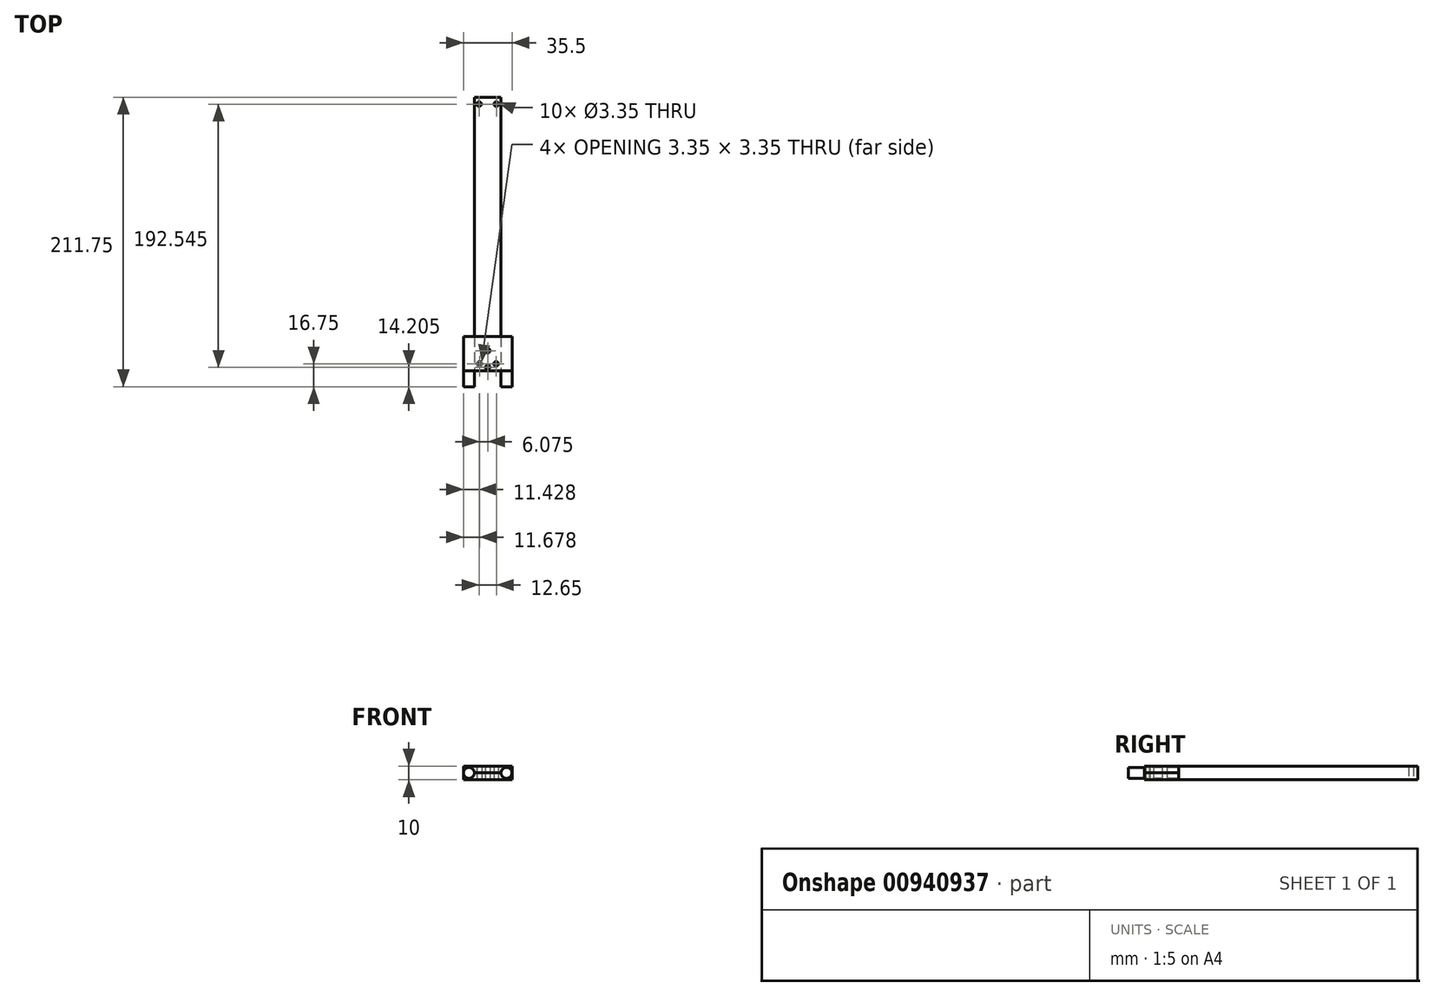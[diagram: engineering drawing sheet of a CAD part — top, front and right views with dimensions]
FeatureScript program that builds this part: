
annotation { "Feature Type Name" : "Feature", "Feature Type Description" : "" }
export const myFeature = defineFeature(function(context is Context, id is Id, definition is map)
    precondition{}
    {
        {
            var Q0;
            Q0=qCreatedBy(makeId("Front.planeOp"),FACE);
            var sketch = newSketch(context, id + "F0", { "sketchPlane" : qUnion([Q0])});
            skLineSegment(sketch, "E0.bottom", {"start": v(-75.87, 17.55) * mm, "end": v(-111.37, 17.55) * mm});
            skLineSegment(sketch, "E0.top", {"start": v(-75.87, 7.55) * mm, "end": v(-111.37, 7.55) * mm});
            skLineSegment(sketch, "E0.left", {"start": v(-75.87, 17.55) * mm, "end": v(-75.87, 7.55) * mm});
            skLineSegment(sketch, "E0.right", {"start": v(-111.37, 17.55) * mm, "end": v(-111.37, 7.55) * mm});
            skLineSegment(sketch, "E1", {"start": v(-75.87, 12.55) * mm, "end": v(-111.37, 12.55) * mm});
            skLineSegment(sketch, "E2", {"start": v(-111.37, 12.55) * mm, "end": v(-107.37, 12.55) * mm});
            skLineSegment(sketch, "E3", {"start": v(-107.37, 12.55) * mm, "end": v(-75.87, 12.55) * mm});
            skLineSegment(sketch, "E4", {"start": v(-75.87, 12.55) * mm, "end": v(-79.87, 12.55) * mm});
            skCircle(sketch, "E5", {"center": v(-107.37, 12.55) * mm, "radius": 4 * mm});
            skCircle(sketch, "E6", {"center": v(-79.87, 12.55) * mm, "radius": 4 * mm});
            skSolve(sketch);
        }
        {
            var Q0;
            {var subQ1=sQuery(id+"F0.wireOp",EDGE,"E1");var subQ3=makeQuery(id+"F0.imprint","IMPRINT",VERTEX,{"disambiguationData":[OD(1.0)],"derivedFrom":subQ1});Q0=makeQuery(id+"F0.imprint","IMPRINT",FACE,{"disambiguationData":[TD([[makeQuery(id+"F0.imprint","IMPRINT",EDGE,{"disambiguationData":[TD([[subQ3,1.0]])],"derivedFrom":subQ1}),-1.0]])]});}
            var Q1;
            {var subQ1=sQuery(id+"F0.wireOp",EDGE,"E1");var subQ3=makeQuery(id+"F0.imprint","IMPRINT",VERTEX,{"disambiguationData":[OD(1.0)],"derivedFrom":subQ1});Q1=makeQuery(id+"F0.imprint","IMPRINT",FACE,{"disambiguationData":[TD([[makeQuery(id+"F0.imprint","IMPRINT",EDGE,{"disambiguationData":[TD([[subQ3,1.0]])],"derivedFrom":subQ1}),1.0]])]});}
            var Q2;
            {var subQ1=sQuery(id+"F0.wireOp",EDGE,"E1");var subQ3=makeQuery(id+"F0.imprint","IMPRINT",VERTEX,{"disambiguationData":[OD(0.0)],"derivedFrom":subQ1});Q2=makeQuery(id+"F0.imprint","IMPRINT",FACE,{"disambiguationData":[TD([[makeQuery(id+"F0.imprint","IMPRINT",EDGE,{"disambiguationData":[TD([[subQ3,-1.0]])],"derivedFrom":subQ1}),-1.0]])]});}
            var Q3;
            {var subQ1=sQuery(id+"F0.wireOp",EDGE,"E1");var subQ3=makeQuery(id+"F0.imprint","IMPRINT",VERTEX,{"disambiguationData":[OD(0.0)],"derivedFrom":subQ1});Q3=makeQuery(id+"F0.imprint","IMPRINT",FACE,{"disambiguationData":[TD([[makeQuery(id+"F0.imprint","IMPRINT",EDGE,{"disambiguationData":[TD([[subQ3,-1.0]])],"derivedFrom":subQ1}),1.0]])]});}
            extrude(context, id + "F1", {"entities" : qUnion([Q0, Q1, Q2, Q3]), "depth" : 11.75 * mm, "offsetDistance" : 25 * mm});
        }
        {
            var Q0;
            {var subQ1=sQuery(id+"F0.wireOp",EDGE,"E0.top");Q0=makeQuery(id+"F0.imprint","IMPRINT",FACE,{"disambiguationData":[TD([[makeQuery(id+"F0.imprint","IMPRINT",EDGE,{"derivedFrom":subQ1}),-1.0]])]});}
            extrude(context, id + "F2", {"entities" : qUnion([Q0]), "oppositeDirection" : true, "depth" : 25 * mm, "offsetDistance" : 25 * mm});
        }
        {
            var Q0;
            {var subQ6=sQuery(id+"F0.wireOp",EDGE,"E0.bottom");Q0=makeQuery(id+"F0.imprint","IMPRINT",FACE,{"disambiguationData":[TD([[makeQuery(id+"F0.imprint","IMPRINT",EDGE,{"derivedFrom":subQ6}),1.0]])]});}
            extrude(context, id + "F3", {"entities" : qUnion([Q0]), "oppositeDirection" : true, "depth" : 25 * mm, "offsetDistance" : 25 * mm});
        }
        {
            var Q0;
            {var subQ1=sQuery(id+"F0.wireOp",EDGE,"E1");var subQ3=makeQuery(id+"F0.imprint","IMPRINT",VERTEX,{"disambiguationData":[OD(1.0)],"derivedFrom":subQ1});Q0=makeQuery(id+"F0.imprint","IMPRINT",FACE,{"disambiguationData":[TD([[makeQuery(id+"F0.imprint","IMPRINT",EDGE,{"disambiguationData":[TD([[subQ3,1.0]])],"derivedFrom":subQ1}),-1.0]])]});}
            var Q1;
            {var subQ1=sQuery(id+"F0.wireOp",EDGE,"E1");var subQ3=makeQuery(id+"F0.imprint","IMPRINT",VERTEX,{"disambiguationData":[OD(1.0)],"derivedFrom":subQ1});Q1=makeQuery(id+"F0.imprint","IMPRINT",FACE,{"disambiguationData":[TD([[makeQuery(id+"F0.imprint","IMPRINT",EDGE,{"disambiguationData":[TD([[subQ3,1.0]])],"derivedFrom":subQ1}),1.0]])]});}
            var Q2;
            {var subQ1=sQuery(id+"F0.wireOp",EDGE,"E1");var subQ3=makeQuery(id+"F0.imprint","IMPRINT",VERTEX,{"disambiguationData":[OD(0.0)],"derivedFrom":subQ1});Q2=makeQuery(id+"F0.imprint","IMPRINT",FACE,{"disambiguationData":[TD([[makeQuery(id+"F0.imprint","IMPRINT",EDGE,{"disambiguationData":[TD([[subQ3,-1.0]])],"derivedFrom":subQ1}),-1.0]])]});}
            var Q3;
            {var subQ1=sQuery(id+"F0.wireOp",EDGE,"E1");var subQ3=makeQuery(id+"F0.imprint","IMPRINT",VERTEX,{"disambiguationData":[OD(0.0)],"derivedFrom":subQ1});Q3=makeQuery(id+"F0.imprint","IMPRINT",FACE,{"disambiguationData":[TD([[makeQuery(id+"F0.imprint","IMPRINT",EDGE,{"disambiguationData":[TD([[subQ3,-1.0]])],"derivedFrom":subQ1}),1.0]])]});}
            extrude(context, id + "F4", {"entities" : qUnion([Q0, Q1, Q2, Q3]), "oppositeDirection" : true, "depth" : 25 * mm, "offsetDistance" : 25 * mm});
        }
        {
            var Q0;
            Q0=makeQuery(id+"F3.opExtrude","CAP_FACE",FACE,{"disambiguationData":[OSD([sQuery(id+"F0.wireOp",EDGE,"E0.bottom"),sQuery(id+"F0.wireOp",EDGE,"E0.left"),sQuery(id+"F0.wireOp",EDGE,"E0.right"),sQuery(id+"F0.wireOp",EDGE,"E1"),sQuery(id+"F0.wireOp",EDGE,"E5"),sQuery(id+"F0.wireOp",EDGE,"E6")])],"isStart":false});
            var sketch = newSketch(context, id + "F5", { "sketchPlane" : qUnion([Q0])});
            skLineSegment(sketch, "E7.bottom", {"start": v(109.37, 7.55) * mm, "end": v(75.87, 7.55) * mm});
            skLineSegment(sketch, "E7.top", {"start": v(109.37, 17.55) * mm, "end": v(75.87, 17.55) * mm});
            skLineSegment(sketch, "E7.left", {"start": v(109.37, 7.55) * mm, "end": v(109.37, 17.55) * mm});
            skLineSegment(sketch, "E7.right", {"start": v(75.87, 7.55) * mm, "end": v(75.87, 17.55) * mm});
            skLineSegment(sketch, "E8", {"start": v(75.87, 12.55) * mm, "end": v(111.37, 12.55) * mm});
            skLineSegment(sketch, "E9", {"start": v(111.37, 12.55) * mm, "end": v(103.37, 12.55) * mm});
            skLineSegment(sketch, "E10", {"start": v(103.37, 12.55) * mm, "end": v(83.87, 12.55) * mm});
            skLineSegment(sketch, "E11", {"start": v(83.87, 12.55) * mm, "end": v(75.87, 12.55) * mm});
            skLineSegment(sketch, "E12", {"start": v(103.37, 12.55) * mm, "end": v(103.37, 7.55) * mm});
            skLineSegment(sketch, "E13", {"start": v(103.37, 7.55) * mm, "end": v(103.37, 17.55) * mm});
            skLineSegment(sketch, "E14", {"start": v(103.37, 17.55) * mm, "end": v(83.87, 17.55) * mm});
            skLineSegment(sketch, "E15", {"start": v(83.87, 17.55) * mm, "end": v(83.87, 7.55) * mm});
            skLineSegment(sketch, "E16", {"start": v(83.87, 7.55) * mm, "end": v(101, 7.55) * mm});
            skLineSegment(sketch, "E17", {"start": v(101, 7.55) * mm, "end": v(103.37, 7.55) * mm});
            skSolve(sketch);
        }
        {
            var Q0;
            {var subQ0=sQuery(id+"F5.wireOp",EDGE,"E13");Q0=makeQuery(id+"F5.imprint","IMPRINT",FACE,{"disambiguationData":[TD([[makeQuery(id+"F5.imprint","IMPRINT",EDGE,{"derivedFrom":subQ0}),1.0]])]});}
            var Q1;
            {var subQ0=sQuery(id+"F5.wireOp",EDGE,"E12");Q1=makeQuery(id+"F5.imprint","IMPRINT",FACE,{"disambiguationData":[TD([[makeQuery(id+"F5.imprint","IMPRINT",EDGE,{"derivedFrom":subQ0}),-1.0]])]});}
            extrude(context, id + "F6", {"entities" : qUnion([Q0, Q1]), "depth" : 175 * mm, "offsetDistance" : 25 * mm});
        }
        {
            var Q0;
            Q0=makeQuery(id+"F2.opExtrude","SWEPT_FACE",FACE,{"disambiguationData":[OSD([sQuery(id+"F0.wireOp",EDGE,"E0.top")])]});
            var sketch = newSketch(context, id + "F7", { "sketchPlane" : qUnion([Q0])});
            skLineSegment(sketch, "E18", {"start": v(-93.62, 0) * mm, "end": v(-93.62, -25) * mm});
            skLineSegment(sketch, "E19", {"start": v(-93.62, -25) * mm, "end": v(-93.62, -5) * mm});
            skLineSegment(sketch, "E20", {"start": v(-93.62, -5) * mm, "end": v(-99.7, -5) * mm});
            skLineSegment(sketch, "E21", {"start": v(-99.7, -5) * mm, "end": v(-87.54, -5) * mm});
            skLineSegment(sketch, "E22", {"start": v(-87.54, -5) * mm, "end": v(-93.62, -5) * mm});
            skLineSegment(sketch, "E23", {"start": v(-93.62, 0) * mm, "end": v(-93.62, -195) * mm});
            skLineSegment(sketch, "E24", {"start": v(-93.62, -195) * mm, "end": v(-99.94, -195) * mm});
            skLineSegment(sketch, "E25", {"start": v(-99.94, -195) * mm, "end": v(-87.3, -195) * mm});
            skLineSegment(sketch, "E26", {"start": v(-87.3, -195) * mm, "end": v(-93.62, -195) * mm});
            skLineSegment(sketch, "E27", {"start": v(-93.62, -8.53) * mm, "end": v(-93.62, -2.45) * mm});
            skLineSegment(sketch, "E28", {"start": v(-93.62, -2.45) * mm, "end": v(-93.62, -14.6) * mm});
            skLineSegment(sketch, "E29", {"start": v(-93.62, -14.6) * mm, "end": v(-93.62, -8.53) * mm});
            skSolve(sketch);
        }
        {
            var Q0;
            Q0=sQuery(id+"F7.wireOp",VERTEX,"E20.end");
            var Q1;
            Q1=sQuery(id+"F7.wireOp",VERTEX,"E21.end");
            var Q2;
            Q2=sQuery(id+"F7.wireOp",VERTEX,"E24.end");
            var Q3;
            Q3=sQuery(id+"F7.wireOp",VERTEX,"E25.end");
            var Q4;
            Q4=sQuery(id+"F7.wireOp",VERTEX,"E28.end");
            var Q5;
            Q5=sQuery(id+"F7.wireOp",VERTEX,"E27.end");
            var Q6;
            Q6=makeQuery(id+"F2.opExtrude","SWEPT_BODY",BODY,{"disambiguationData":[OSD([sQuery(id+"F0.wireOp",EDGE,"E0.top"),sQuery(id+"F0.wireOp",EDGE,"E0.left"),sQuery(id+"F0.wireOp",EDGE,"E0.right"),sQuery(id+"F0.wireOp",EDGE,"E1"),sQuery(id+"F0.wireOp",EDGE,"E5"),sQuery(id+"F0.wireOp",EDGE,"E6")])]});
            var Q7;
            Q7=makeQuery(id+"F3.opExtrude","SWEPT_BODY",BODY,{"disambiguationData":[OSD([sQuery(id+"F0.wireOp",EDGE,"E0.bottom"),sQuery(id+"F0.wireOp",EDGE,"E0.left"),sQuery(id+"F0.wireOp",EDGE,"E0.right"),sQuery(id+"F0.wireOp",EDGE,"E1"),sQuery(id+"F0.wireOp",EDGE,"E5"),sQuery(id+"F0.wireOp",EDGE,"E6")])]});
            var Q8;
            Q8=makeQuery(id+"F6.opExtrude","SWEPT_BODY",BODY,{"disambiguationData":[OSD([sQuery(id+"F5.wireOp",EDGE,"E7.bottom"),sQuery(id+"F5.wireOp",EDGE,"E7.top"),sQuery(id+"F5.wireOp",EDGE,"E12"),sQuery(id+"F5.wireOp",EDGE,"E13"),sQuery(id+"F5.wireOp",EDGE,"E15")])]});
            hole(context, id + "F8", {"style" : HoleStyle.SIMPLE, "endStyle" : HoleEndStyle.BLIND, "holeDiameter" : 3.35 * mm, "majorDiameter" : 5 * mm, "holeDepth" : 10 * mm, "isTappedThrough" : true, "tappedDepth" : 12 * mm, "tapClearance" : 3, "locations" : qUnion([Q0, Q1, Q2, Q3, Q4, Q5]), "scope" : qUnion([Q6, Q7, Q8])});
        }
    });
